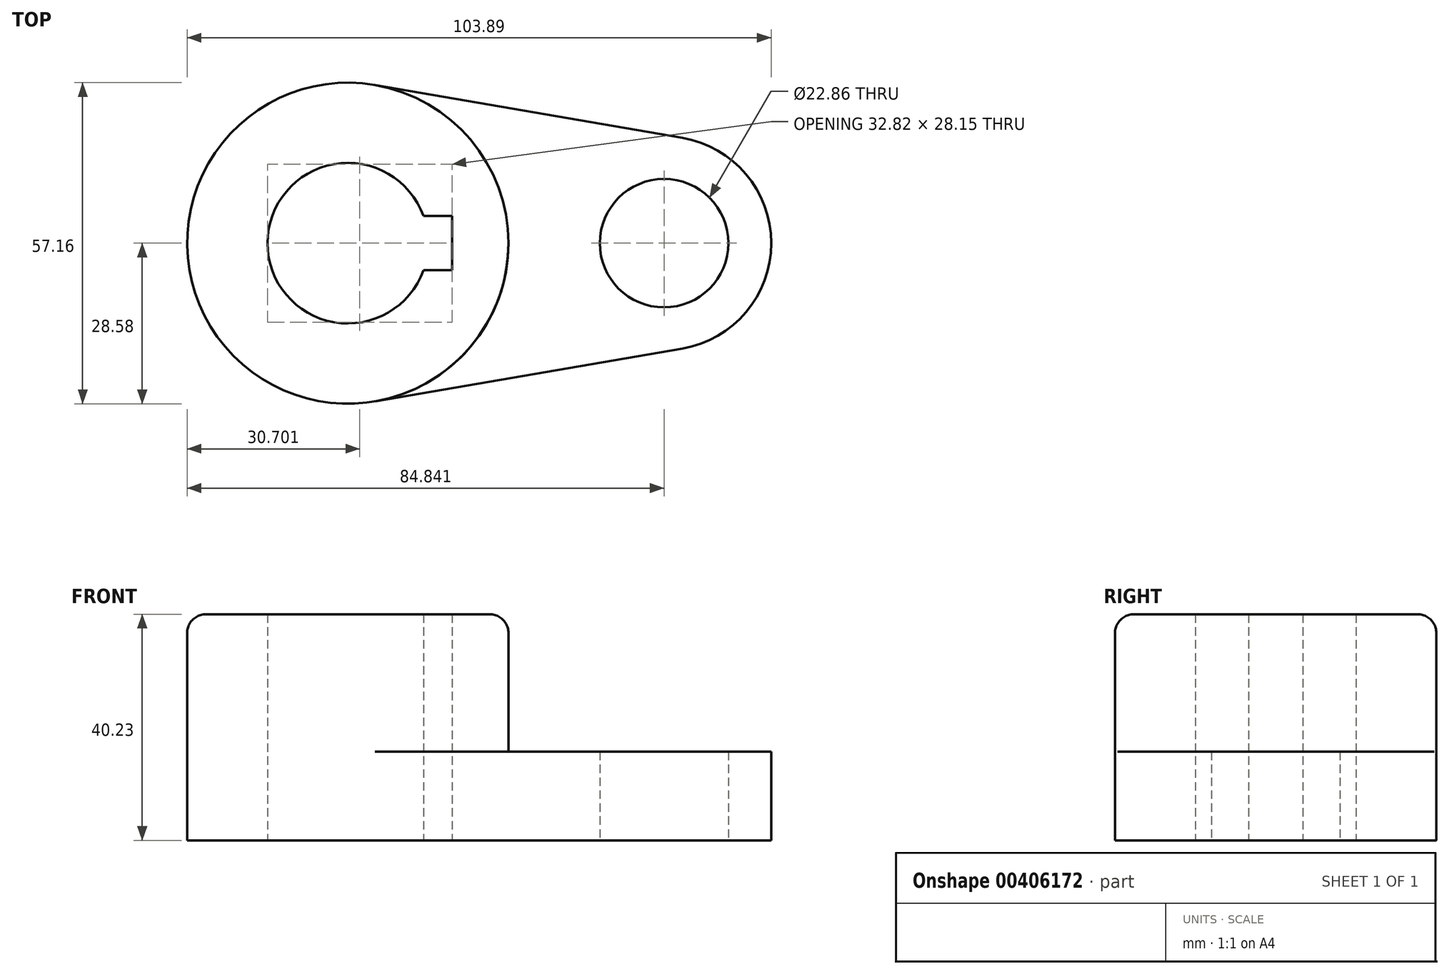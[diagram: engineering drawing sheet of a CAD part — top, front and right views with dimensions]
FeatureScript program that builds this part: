
annotation { "Feature Type Name" : "Feature", "Feature Type Description" : "" }
export const myFeature = defineFeature(function(context is Context, id is Id, definition is map)
    precondition{}
    {
        {
            var Q0;
            Q0=qCreatedBy(makeId("Top.planeOp"),FACE);
            var sketch = newSketch(context, id + "F0", { "sketchPlane" : qUnion([Q0])});
            skCircle(sketch, "E0", {"center": v(0, 0) * mm, "radius": 28.58 * mm});
            skCircle(sketch, "E1", {"center": v(56.26, 0) * mm, "radius": 19.05 * mm});
            skLineSegment(sketch, "E2", {"start": v(4.84, 28.16) * mm, "end": v(59.49, 18.78) * mm});
            skLineSegment(sketch, "E3", {"start": v(59.49, -18.78) * mm, "end": v(4.84, -28.16) * mm});
            skCircle(sketch, "E4", {"center": v(56.26, 0) * mm, "radius": 11.43 * mm});
            skCircle(sketch, "E5", {"center": v(0, 0) * mm, "radius": 14.29 * mm});
            skLineSegment(sketch, "E6.bottom", {"start": v(-18.53, 4.83) * mm, "end": v(18.53, 4.83) * mm});
            skLineSegment(sketch, "E6.top", {"start": v(-18.53, -4.83) * mm, "end": v(18.53, -4.83) * mm});
            skLineSegment(sketch, "E6.left", {"start": v(-18.53, 4.83) * mm, "end": v(-18.53, -4.83) * mm});
            skLineSegment(sketch, "E6.right", {"start": v(18.53, 4.83) * mm, "end": v(18.53, -4.83) * mm});
            skSolve(sketch);
        }
        {
            var Q0;
            {var subQ0=sQuery(id+"F0.wireOp",EDGE,"E2");Q0=makeQuery(id+"F0.imprint","IMPRINT",FACE,{"disambiguationData":[TD([[makeQuery(id+"F0.imprint","IMPRINT",EDGE,{"derivedFrom":subQ0}),-1.0]])]});}
            var Q1;
            Q1=makeQuery(id+"F0.imprint","IMPRINT",FACE,{"disambiguationData":[TD([[makeQuery(id+"F0.imprint","IMPRINT",EDGE,{"derivedFrom":sQuery(id+"F0.wireOp",EDGE,"E4")}),-1.0]])]});
            extrude(context, id + "F1", {"entities" : qUnion([Q0, Q1]), "depth" : 15.77 * mm});
        }
        {
            var Q0;
            Q0=makeQuery(id+"F0.imprint","IMPRINT",FACE,{"disambiguationData":[TD([[makeQuery(id+"F0.imprint","IMPRINT",EDGE,{"derivedFrom":sQuery(id+"F0.wireOp",EDGE,"E5")}),-1.0]])]});
            var Q1;
            {var subQ5=sQuery(id+"F0.wireOp",EDGE,"E6.left");Q1=makeQuery(id+"F0.imprint","IMPRINT",FACE,{"disambiguationData":[TD([[makeQuery(id+"F0.imprint","IMPRINT",EDGE,{"derivedFrom":subQ5}),1.0]])]});}
            extrude(context, id + "F2", {"entities" : qUnion([Q0, Q1]), "operationType" : NewBodyOperationType.ADD, "depth" : 40.23 * mm});
        }
        {
            var Q0;
            Q0=makeQuery(id+"F2.opExtrude","CAP_EDGE",EDGE,{"disambiguationData":[OSD([sQuery(id+"F0.wireOp",EDGE,"E0")])],"isStart":false});
            fillet(context, id + "F3", {"entities" : qUnion([Q0]), "radius" : 3.3 * mm, "tangentPropagation" : true, "allowEdgeOverflow" : false});
        }
    });
